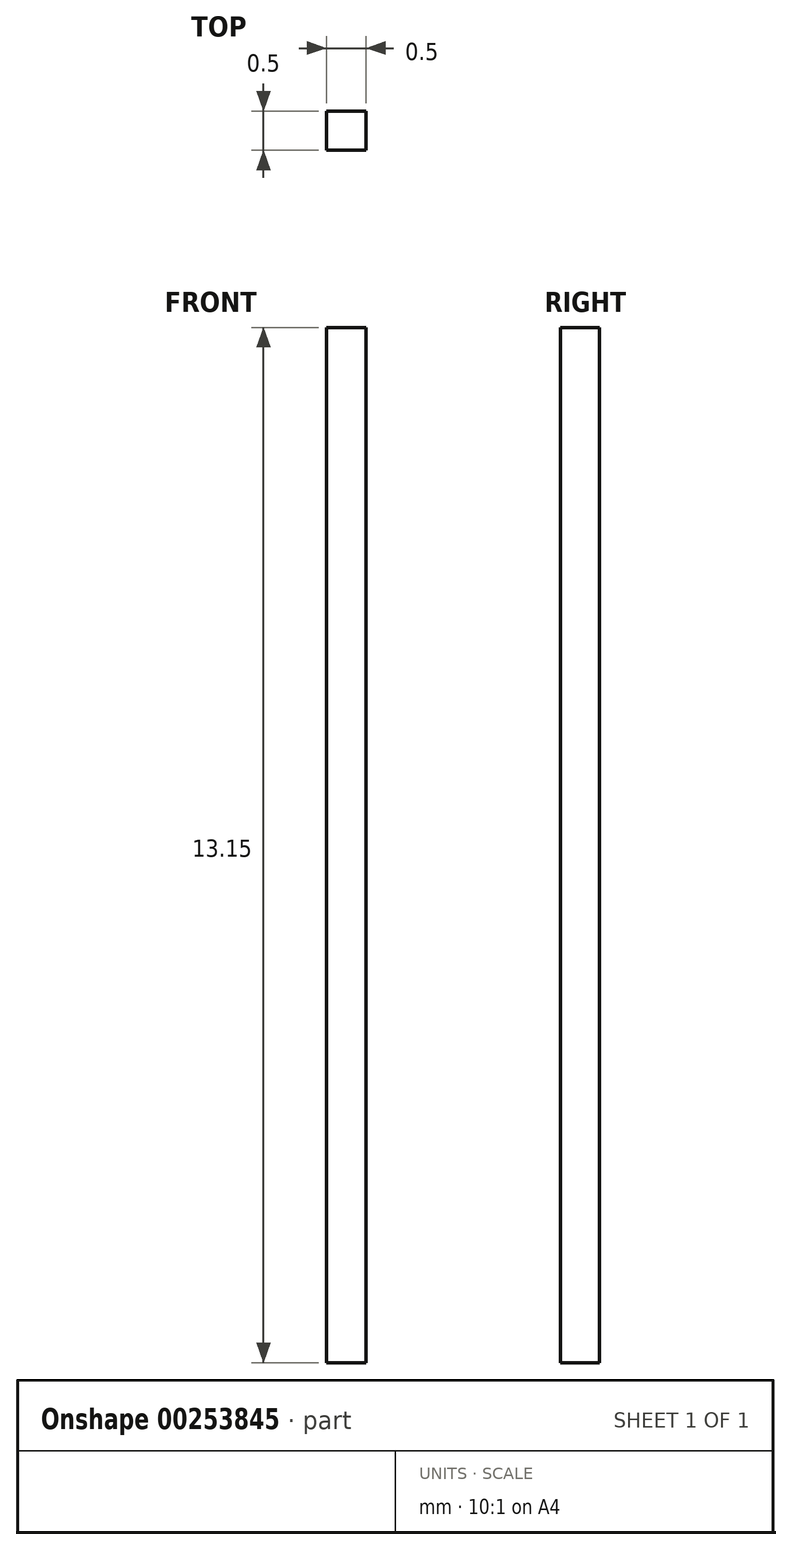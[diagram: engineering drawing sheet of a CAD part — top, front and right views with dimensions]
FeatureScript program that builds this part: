
annotation { "Feature Type Name" : "Feature", "Feature Type Description" : "" }
export const myFeature = defineFeature(function(context is Context, id is Id, definition is map)
    precondition{}
    {
        {
            var Q0;
            Q0=qCreatedBy(makeId("Top.planeOp"),FACE);
            var sketch = newSketch(context, id + "F0", { "sketchPlane" : qUnion([Q0])});
            skLineSegment(sketch, "E0.bottom", {"start": v(0, 0) * mm, "end": v(0.5, 0) * mm});
            skLineSegment(sketch, "E0.top", {"start": v(0, 0.5) * mm, "end": v(0.5, 0.5) * mm});
            skLineSegment(sketch, "E0.left", {"start": v(0, 0) * mm, "end": v(0, 0.5) * mm});
            skLineSegment(sketch, "E0.right", {"start": v(0.5, 0) * mm, "end": v(0.5, 0.5) * mm});
            skSolve(sketch);
        }
        {
            var Q0;
            Q0 = qSketchRegion(id + "F0", true);
            extrude(context, id + "F1", {"entities" : qUnion([Q0]), "depth" : 13.15 * mm});
        }
    });
